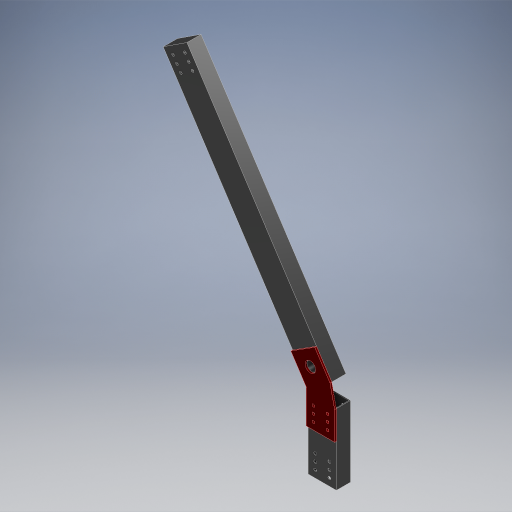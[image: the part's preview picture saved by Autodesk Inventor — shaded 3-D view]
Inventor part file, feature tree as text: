
AUTODESK INVENTOR PART (.ipt)
format: ipt  version: 2024.2 (Build 282272000, 272)  size: 415,744 bytes
history: native  units: in
note: dims shown in document units (in); Inventor stores cm internally (conversion verified against a paired STEP export)
features: extrude x4, other x3, sketch x3, projected_geometry x3
ambient origin geometry x8: Origin, YZ Plane, XZ Plane, XY Plane, X Axis, Y Axis, Z Axis, Center Point
bodies: Body1 (feature_tree), Body2 (feature_tree), Body3 (feature_tree)
feature tree (13):
  other  "Shootaur-Structure"
  sketch  "Sketch1"  dims[d0=27.0in d1=2.0in]
  extrude  "Extrusion8"  Depth=2.0in
  extrude  "Extrusion9"  Depth=5.0in
  extrude  "Extrusion10"  Depth=0.0625in
  extrude  "Extrusion11"  Depth=1.0in
  other  "Back-Support"
  sketch  "Sketch7"  dims[d5=5.0in d21=0.196in]
  projected_geometry  "Projected Loop5"
  projected_geometry  "Projected Loop6"
  other  "Dead-Axle-Gusset"
  sketch  "Sketch8"  dims[d22=0.5in d23=0.5in d24=0.7874in d26=1.0in d27=1.1811in d29=0.5in d60=2.0in d61=2.0in d62=0.196in d63=0.5in d64=0.5in d65=0.7874in d67=1.0in d68=1.1811in d70=0.5in d73=0.75in d74=1.0in d75=1.0in d76=1.0in d77=0.0in d78=1.0in d79=0.0in d80=2.0in d81=2.0in d82=0.125in d83=0.0in d84=0.0625in d85=8.25in d86=0.0in d46=0.5in d47=0.0344in d48=0.5in d49=0.0344in d50=0.5in d51=0.0344in d52=0.5in d53=0.0344in d54=0.5in d55=0.0344in]
  projected_geometry  "Projected Loop7"
